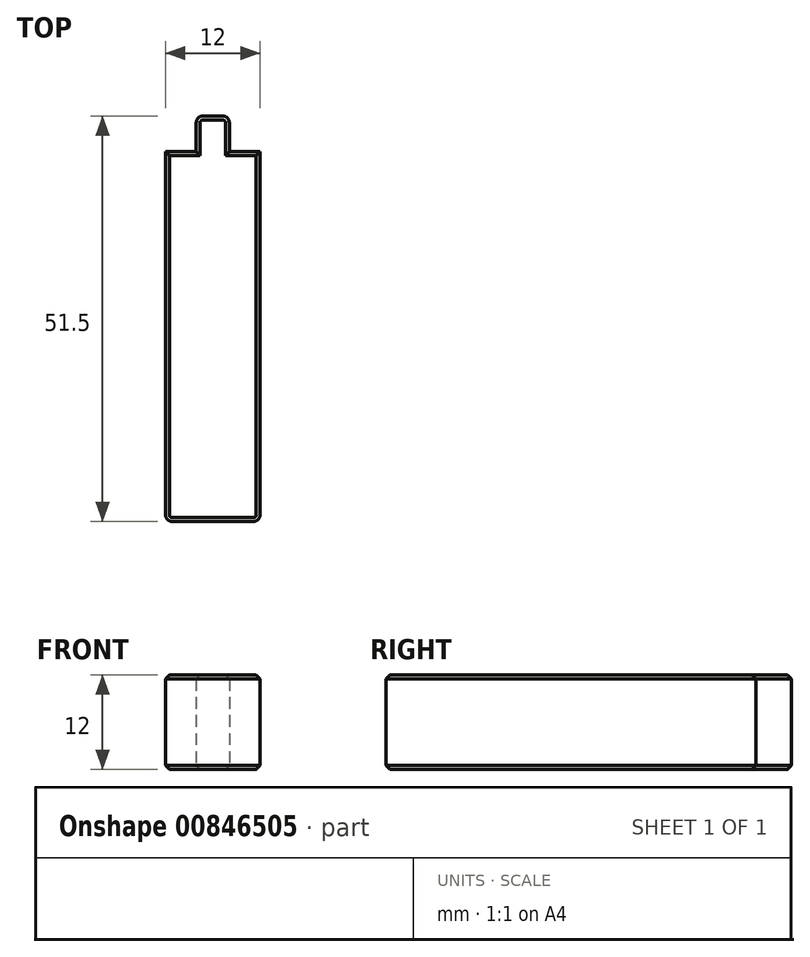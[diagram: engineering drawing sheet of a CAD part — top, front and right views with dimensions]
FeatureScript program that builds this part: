
annotation { "Feature Type Name" : "Feature", "Feature Type Description" : "" }
export const myFeature = defineFeature(function(context is Context, id is Id, definition is map)
    precondition{}
    {
        {
            var Q0;
            Q0=qCreatedBy(makeId("Top.planeOp"),FACE);
            var sketch = newSketch(context, id + "F0", { "sketchPlane" : qUnion([Q0])});
            skLineSegment(sketch, "E0.bottom", {"start": v(6, 23.5) * mm, "end": v(-6, 23.5) * mm});
            skLineSegment(sketch, "E0.top", {"start": v(6, -23.5) * mm, "end": v(-6, -23.5) * mm});
            skLineSegment(sketch, "E0.left", {"start": v(6, 23.5) * mm, "end": v(6, -23.5) * mm});
            skLineSegment(sketch, "E0.right", {"start": v(-6, 23.5) * mm, "end": v(-6, -23.5) * mm});
            skPoint(sketch, "E0.middle", {"position": v(0, 0) * mm});
            skLineSegment(sketch, "E1.bottom", {"start": v(2.1, 28) * mm, "end": v(-2.1, 28) * mm});
            skLineSegment(sketch, "E1.top", {"start": v(2.1, 19) * mm, "end": v(-2.1, 19) * mm});
            skLineSegment(sketch, "E1.left", {"start": v(2.1, 28) * mm, "end": v(2.1, 19) * mm});
            skLineSegment(sketch, "E1.right", {"start": v(-2.1, 28) * mm, "end": v(-2.1, 19) * mm});
            skPoint(sketch, "E1.middle", {"position": v(0, 23.5) * mm});
            skSolve(sketch);
        }
        {
            var Q0;
            Q0 = qSketchRegion(id + "F0", true);
            extrude(context, id + "F1", {"entities" : qUnion([Q0]), "depth" : 12 * mm, "offsetDistance" : 25 * mm});
        }
        {
            var Q0;
            Q0=makeQuery(id+"F1.opExtrude","SWEPT_EDGE",EDGE,{"disambiguationData":[OSD([sQuery(id+"F0.wireOp",EDGE,"E1.bottom"),sQuery(id+"F0.wireOp",EDGE,"E1.left")])]});
            var Q1;
            Q1=makeQuery(id+"F1.opExtrude","SWEPT_EDGE",EDGE,{"disambiguationData":[OSD([sQuery(id+"F0.wireOp",EDGE,"E1.bottom"),sQuery(id+"F0.wireOp",EDGE,"E1.right")])]});
            var Q2;
            Q2=makeQuery(id+"F1.opExtrude","SWEPT_EDGE",EDGE,{"disambiguationData":[OSD([sQuery(id+"F0.wireOp",EDGE,"E0.top"),sQuery(id+"F0.wireOp",EDGE,"E0.left")])]});
            var Q3;
            Q3=makeQuery(id+"F1.opExtrude","SWEPT_EDGE",EDGE,{"disambiguationData":[OSD([sQuery(id+"F0.wireOp",EDGE,"E0.top"),sQuery(id+"F0.wireOp",EDGE,"E0.right")])]});
            fillet(context, id + "F2", {"entities" : qUnion([Q0, Q1, Q2, Q3]), "radius" : 0.8 * mm, "tangentPropagation" : true, "allowEdgeOverflow" : false});
        }
        {
            var Q0;
            Q0=makeQuery(id+"F1.opExtrude","CAP_FACE",FACE,{"disambiguationData":[OSD([sQuery(id+"F0.wireOp",EDGE,"E0.bottom"),sQuery(id+"F0.wireOp",EDGE,"E0.top"),sQuery(id+"F0.wireOp",EDGE,"E0.left"),sQuery(id+"F0.wireOp",EDGE,"E0.right"),sQuery(id+"F0.wireOp",EDGE,"E1.bottom"),sQuery(id+"F0.wireOp",EDGE,"E1.left"),sQuery(id+"F0.wireOp",EDGE,"E1.right")])],"isStart":false});
            var Q1;
            Q1=makeQuery(id+"F1.opExtrude","CAP_FACE",FACE,{"disambiguationData":[OSD([sQuery(id+"F0.wireOp",EDGE,"E0.bottom"),sQuery(id+"F0.wireOp",EDGE,"E0.top"),sQuery(id+"F0.wireOp",EDGE,"E0.left"),sQuery(id+"F0.wireOp",EDGE,"E0.right"),sQuery(id+"F0.wireOp",EDGE,"E1.bottom"),sQuery(id+"F0.wireOp",EDGE,"E1.left"),sQuery(id+"F0.wireOp",EDGE,"E1.right")])],"isStart":true});
            chamfer(context, id + "F3", {"entities" : qUnion([Q0, Q1]), "width" : 0.5 * mm, "tangentPropagation" : true});
        }
    });
